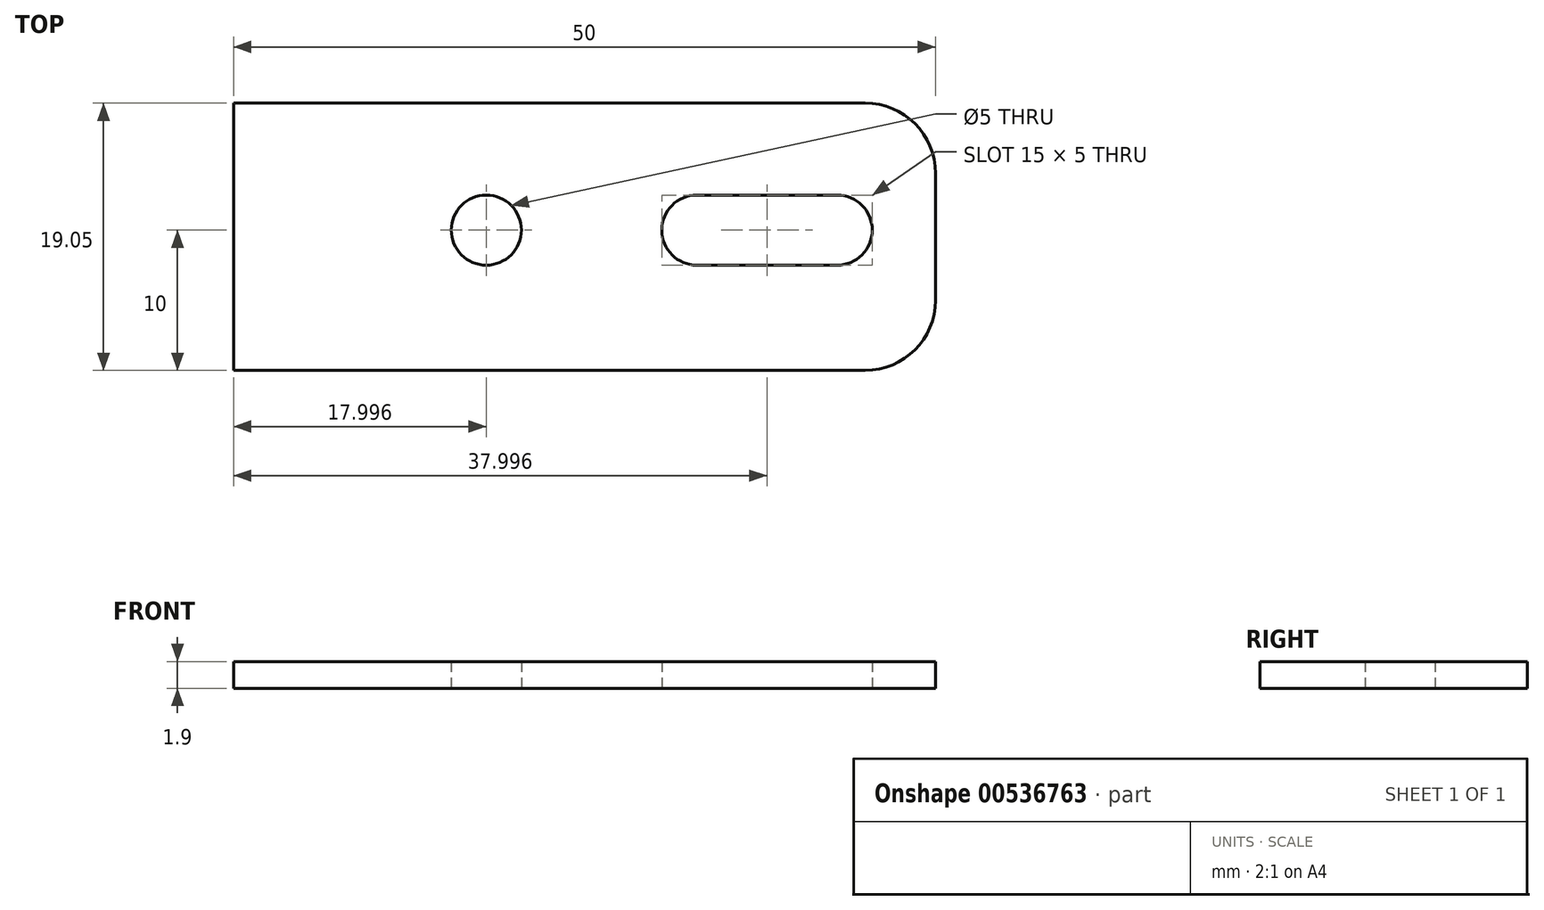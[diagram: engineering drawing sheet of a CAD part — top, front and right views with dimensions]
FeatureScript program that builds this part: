
annotation { "Feature Type Name" : "Feature", "Feature Type Description" : "" }
export const myFeature = defineFeature(function(context is Context, id is Id, definition is map)
    precondition{}
    {
        {
            var Q0;
            Q0=qCreatedBy(makeId("Top.planeOp"),FACE);
            var sketch = newSketch(context, id + "F0", { "sketchPlane" : qUnion([Q0])});
            skLineSegment(sketch, "E0.bottom", {"start": v(-32.85, 9.05) * mm, "end": v(12.15, 9.05) * mm});
            skLineSegment(sketch, "E0.top", {"start": v(-32.85, -10) * mm, "end": v(12.15, -10) * mm});
            skLineSegment(sketch, "E0.left", {"start": v(-32.85, 9.05) * mm, "end": v(-32.85, -10) * mm});
            skLineSegment(sketch, "E0.right", {"start": v(17.15, 4.05) * mm, "end": v(17.15, -5) * mm});
            skArc(sketch, "E1.filletArc", {"start": v(17.15, 4.05) * mm, "mid": v(15.68, 7.59) * mm, "end": v(12.15, 9.05) * mm});
            skArc(sketch, "E2.filletArc", {"start": v(12.15, -10) * mm, "mid": v(15.68, -8.54) * mm, "end": v(17.15, -5) * mm});
            skArc(sketch, "E3", {"start": v(10.15, -2.5) * mm, "mid": v(12.65, 0) * mm, "end": v(10.15, 2.5) * mm});
            skArc(sketch, "E4", {"start": v(0.15, 2.5) * mm, "mid": v(-2.35, 0) * mm, "end": v(0.15, -2.5) * mm});
            skLineSegment(sketch, "E5", {"start": v(0.15, 2.5) * mm, "end": v(10.15, 2.5) * mm});
            skLineSegment(sketch, "E6", {"start": v(0.15, -2.5) * mm, "end": v(10.15, -2.5) * mm});
            skCircle(sketch, "E7", {"center": v(-14.85, 0) * mm, "radius": 2.5 * mm});
            skSolve(sketch);
        }
        {
            var Q0;
            Q0 = qSketchRegion(id + "F0", true);
            extrude(context, id + "F1", {"entities" : qUnion([Q0]), "depth" : 1.9 * mm, "offsetDistance" : 25 * mm});
        }
    });
